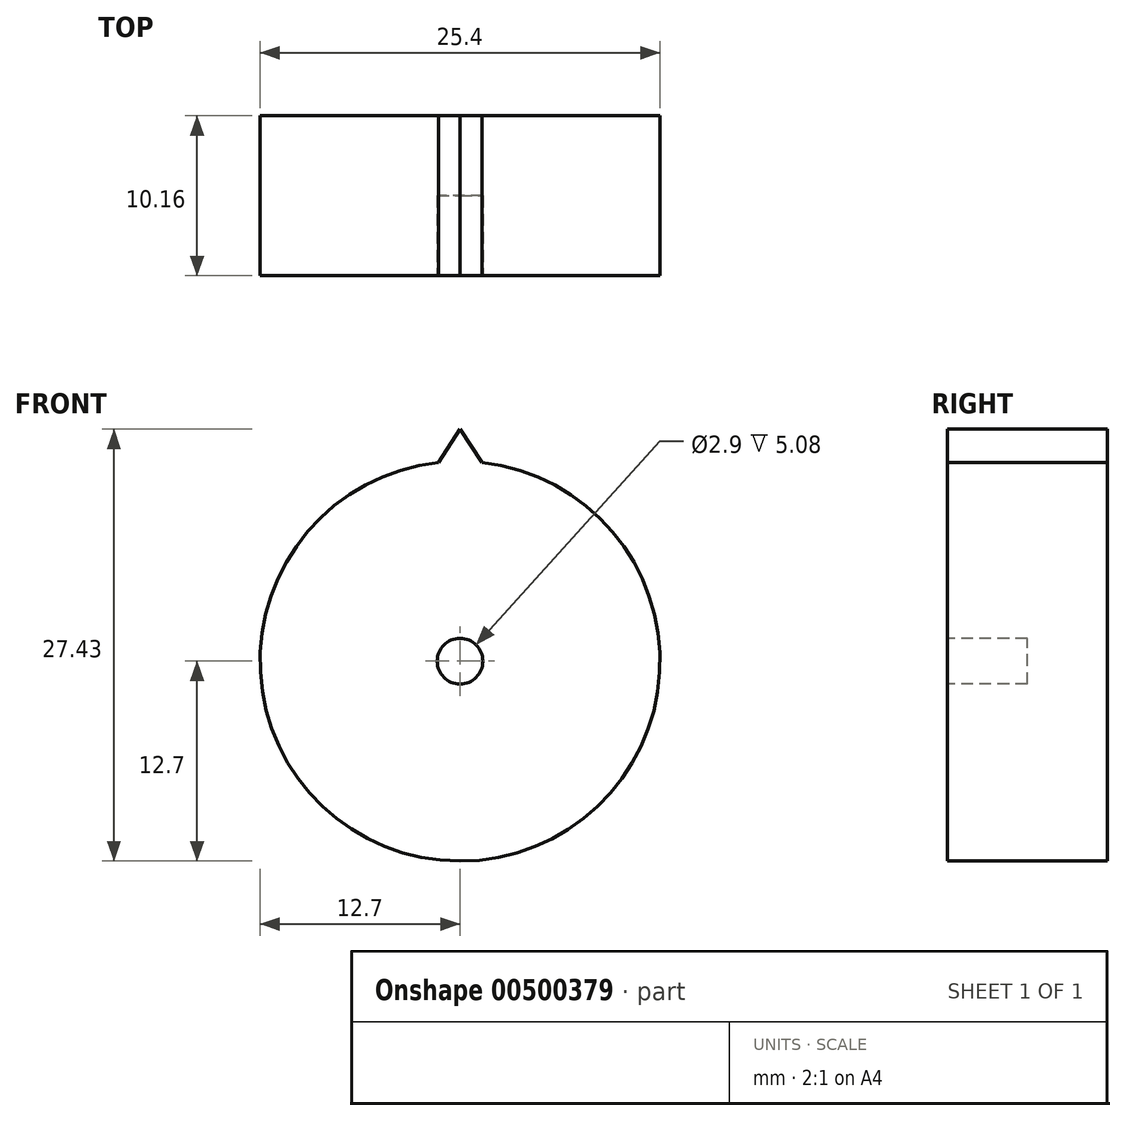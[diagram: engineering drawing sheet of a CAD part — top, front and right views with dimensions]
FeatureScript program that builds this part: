
annotation { "Feature Type Name" : "Feature", "Feature Type Description" : "" }
export const myFeature = defineFeature(function(context is Context, id is Id, definition is map)
    precondition{}
    {
        {
            var Q0;
            Q0=qCreatedBy(makeId("Front.planeOp"),FACE);
            var sketch = newSketch(context, id + "F0", { "sketchPlane" : qUnion([Q0])});
            skCircle(sketch, "E0", {"center": v(0, 0) * mm, "radius": 12.7 * mm});
            skLineSegment(sketch, "E1", {"start": v(-1.36, 12.63) * mm, "end": v(0, 14.73) * mm});
            skLineSegment(sketch, "E2", {"start": v(0, 14.73) * mm, "end": v(1.38, 12.62) * mm});
            skLineSegment(sketch, "E3", {"start": v(-1.36, 12.63) * mm, "end": v(1.38, 12.62) * mm});
            skSolve(sketch);
        }
        {
            var Q0;
            Q0=makeQuery(id+"F0.imprint","IMPRINT",FACE,{"disambiguationData":[TD([[makeQuery(id+"F0.imprint","IMPRINT",EDGE,{"derivedFrom":sQuery(id+"F0.wireOp",EDGE,"E0")}),1.0]])]});
            extrude(context, id + "F1", {"entities" : qUnion([Q0]), "depth" : 10.16 * mm});
        }
        {
            var Q0;
            {var subQ1=sQuery(id+"F0.wireOp",EDGE,"E1");Q0=makeQuery(id+"F0.imprint","IMPRINT",FACE,{"disambiguationData":[TD([[makeQuery(id+"F0.imprint","IMPRINT",EDGE,{"derivedFrom":subQ1}),-1.0]])]});}
            extrude(context, id + "F2", {"entities" : qUnion([Q0]), "operationType" : NewBodyOperationType.ADD, "depth" : 10.16 * mm});
        }
        {
            var Q0;
            {var subQ0=sQuery(id+"F0.wireOp",EDGE,"E2");var subQ1=sQuery(id+"F0.wireOp",EDGE,"E1");var subQ2=sQuery(id+"F0.wireOp",EDGE,"E0");Q0=makeQuery(id+"FW0Evy0XLkxjWks_1.31.F2.boolean.opBoolean","MERGE",FACE,{"derivedFrom":[makeQuery(id+"FW0Evy0XLkxjWks_1.30.F2.boolean.opBoolean","MERGE",FACE,{"derivedFrom":[makeQuery(id+"FW0Evy0XLkxjWks_1.29.F2.boolean.opBoolean","MERGE",FACE,{"derivedFrom":[makeQuery(id+"FW0Evy0XLkxjWks_1.28.F2.boolean.opBoolean","MERGE",FACE,{"derivedFrom":[makeQuery(id+"FW0Evy0XLkxjWks_1.27.F2.boolean.opBoolean","MERGE",FACE,{"derivedFrom":[makeQuery(id+"FW0Evy0XLkxjWks_1.26.F2.boolean.opBoolean","MERGE",FACE,{"derivedFrom":[makeQuery(id+"FW0Evy0XLkxjWks_1.25.F2.boolean.opBoolean","MERGE",FACE,{"derivedFrom":[makeQuery(id+"FW0Evy0XLkxjWks_1.24.F2.boolean.opBoolean","MERGE",FACE,{"derivedFrom":[makeQuery(id+"FW0Evy0XLkxjWks_1.23.F2.boolean.opBoolean","MERGE",FACE,{"derivedFrom":[makeQuery(id+"FW0Evy0XLkxjWks_1.22.F2.boolean.opBoolean","MERGE",FACE,{"derivedFrom":[makeQuery(id+"FW0Evy0XLkxjWks_1.21.F2.boolean.opBoolean","MERGE",FACE,{"derivedFrom":[makeQuery(id+"FW0Evy0XLkxjWks_1.20.F2.boolean.opBoolean","MERGE",FACE,{"derivedFrom":[makeQuery(id+"FW0Evy0XLkxjWks_1.19.F2.boolean.opBoolean","MERGE",FACE,{"derivedFrom":[makeQuery(id+"FW0Evy0XLkxjWks_1.18.F2.boolean.opBoolean","MERGE",FACE,{"derivedFrom":[makeQuery(id+"FW0Evy0XLkxjWks_1.17.F2.boolean.opBoolean","MERGE",FACE,{"derivedFrom":[makeQuery(id+"FW0Evy0XLkxjWks_1.16.F2.boolean.opBoolean","MERGE",FACE,{"derivedFrom":[makeQuery(id+"FW0Evy0XLkxjWks_1.15.F2.boolean.opBoolean","MERGE",FACE,{"derivedFrom":[makeQuery(id+"FW0Evy0XLkxjWks_1.14.F2.boolean.opBoolean","MERGE",FACE,{"derivedFrom":[makeQuery(id+"FW0Evy0XLkxjWks_1.13.F2.boolean.opBoolean","MERGE",FACE,{"derivedFrom":[makeQuery(id+"FW0Evy0XLkxjWks_1.12.F2.boolean.opBoolean","MERGE",FACE,{"derivedFrom":[makeQuery(id+"FW0Evy0XLkxjWks_1.11.F2.boolean.opBoolean","MERGE",FACE,{"derivedFrom":[makeQuery(id+"FW0Evy0XLkxjWks_1.10.F2.boolean.opBoolean","MERGE",FACE,{"derivedFrom":[makeQuery(id+"FW0Evy0XLkxjWks_1.9.F2.boolean.opBoolean","MERGE",FACE,{"derivedFrom":[makeQuery(id+"FW0Evy0XLkxjWks_1.8.F2.boolean.opBoolean","MERGE",FACE,{"derivedFrom":[makeQuery(id+"FW0Evy0XLkxjWks_1.7.F2.boolean.opBoolean","MERGE",FACE,{"derivedFrom":[makeQuery(id+"FW0Evy0XLkxjWks_1.6.F2.boolean.opBoolean","MERGE",FACE,{"derivedFrom":[makeQuery(id+"FW0Evy0XLkxjWks_1.5.F2.boolean.opBoolean","MERGE",FACE,{"derivedFrom":[makeQuery(id+"FW0Evy0XLkxjWks_1.4.F2.boolean.opBoolean","MERGE",FACE,{"derivedFrom":[makeQuery(id+"FW0Evy0XLkxjWks_1.3.F2.boolean.opBoolean","MERGE",FACE,{"derivedFrom":[makeQuery(id+"FW0Evy0XLkxjWks_1.2.F2.boolean.opBoolean","MERGE",FACE,{"derivedFrom":[makeQuery(id+"FW0Evy0XLkxjWks_1.1.F2.boolean.opBoolean","MERGE",FACE,{"derivedFrom":[makeQuery(id+"F2.boolean.opBoolean","MERGE",FACE,{"derivedFrom":[makeQuery(id+"F1.opExtrude","CAP_FACE",FACE,{"disambiguationData":[OSD([subQ2])],"isStart":false}),makeQuery(id+"F2.opExtrude","CAP_FACE",FACE,{"disambiguationData":[OSD([subQ2,subQ1,subQ0])],"isStart":false})]}),makeQuery(id+"FW0Evy0XLkxjWks_1.1.F2.opExtrude","CAP_FACE",FACE,{"disambiguationData":[OSD([subQ2,subQ1,subQ0])],"isStart":false})]}),makeQuery(id+"FW0Evy0XLkxjWks_1.2.F2.opExtrude","CAP_FACE",FACE,{"disambiguationData":[OSD([subQ2,subQ1,subQ0])],"isStart":false})]}),makeQuery(id+"FW0Evy0XLkxjWks_1.3.F2.opExtrude","CAP_FACE",FACE,{"disambiguationData":[OSD([subQ2,subQ1,subQ0])],"isStart":false})]}),makeQuery(id+"FW0Evy0XLkxjWks_1.4.F2.opExtrude","CAP_FACE",FACE,{"disambiguationData":[OSD([subQ2,subQ1,subQ0])],"isStart":false})]}),makeQuery(id+"FW0Evy0XLkxjWks_1.5.F2.opExtrude","CAP_FACE",FACE,{"disambiguationData":[OSD([subQ2,subQ1,subQ0])],"isStart":false})]}),makeQuery(id+"FW0Evy0XLkxjWks_1.6.F2.opExtrude","CAP_FACE",FACE,{"disambiguationData":[OSD([subQ2,subQ1,subQ0])],"isStart":false})]}),makeQuery(id+"FW0Evy0XLkxjWks_1.7.F2.opExtrude","CAP_FACE",FACE,{"disambiguationData":[OSD([subQ2,subQ1,subQ0])],"isStart":false})]}),makeQuery(id+"FW0Evy0XLkxjWks_1.8.F2.opExtrude","CAP_FACE",FACE,{"disambiguationData":[OSD([subQ2,subQ1,subQ0])],"isStart":false})]}),makeQuery(id+"FW0Evy0XLkxjWks_1.9.F2.opExtrude","CAP_FACE",FACE,{"disambiguationData":[OSD([subQ2,subQ1,subQ0])],"isStart":false})]}),makeQuery(id+"FW0Evy0XLkxjWks_1.10.F2.opExtrude","CAP_FACE",FACE,{"disambiguationData":[OSD([subQ2,subQ1,subQ0])],"isStart":false})]}),makeQuery(id+"FW0Evy0XLkxjWks_1.11.F2.opExtrude","CAP_FACE",FACE,{"disambiguationData":[OSD([subQ2,subQ1,subQ0])],"isStart":false})]}),makeQuery(id+"FW0Evy0XLkxjWks_1.12.F2.opExtrude","CAP_FACE",FACE,{"disambiguationData":[OSD([subQ2,subQ1,subQ0])],"isStart":false})]}),makeQuery(id+"FW0Evy0XLkxjWks_1.13.F2.opExtrude","CAP_FACE",FACE,{"disambiguationData":[OSD([subQ2,subQ1,subQ0])],"isStart":false})]}),makeQuery(id+"FW0Evy0XLkxjWks_1.14.F2.opExtrude","CAP_FACE",FACE,{"disambiguationData":[OSD([subQ2,subQ1,subQ0])],"isStart":false})]}),makeQuery(id+"FW0Evy0XLkxjWks_1.15.F2.opExtrude","CAP_FACE",FACE,{"disambiguationData":[OSD([subQ2,subQ1,subQ0])],"isStart":false})]}),makeQuery(id+"FW0Evy0XLkxjWks_1.16.F2.opExtrude","CAP_FACE",FACE,{"disambiguationData":[OSD([subQ2,subQ1,subQ0])],"isStart":false})]}),makeQuery(id+"FW0Evy0XLkxjWks_1.17.F2.opExtrude","CAP_FACE",FACE,{"disambiguationData":[OSD([subQ2,subQ1,subQ0])],"isStart":false})]}),makeQuery(id+"FW0Evy0XLkxjWks_1.18.F2.opExtrude","CAP_FACE",FACE,{"disambiguationData":[OSD([subQ2,subQ1,subQ0])],"isStart":false})]}),makeQuery(id+"FW0Evy0XLkxjWks_1.19.F2.opExtrude","CAP_FACE",FACE,{"disambiguationData":[OSD([subQ2,subQ1,subQ0])],"isStart":false})]}),makeQuery(id+"FW0Evy0XLkxjWks_1.20.F2.opExtrude","CAP_FACE",FACE,{"disambiguationData":[OSD([subQ2,subQ1,subQ0])],"isStart":false})]}),makeQuery(id+"FW0Evy0XLkxjWks_1.21.F2.opExtrude","CAP_FACE",FACE,{"disambiguationData":[OSD([subQ2,subQ1,subQ0])],"isStart":false})]}),makeQuery(id+"FW0Evy0XLkxjWks_1.22.F2.opExtrude","CAP_FACE",FACE,{"disambiguationData":[OSD([subQ2,subQ1,subQ0])],"isStart":false})]}),makeQuery(id+"FW0Evy0XLkxjWks_1.23.F2.opExtrude","CAP_FACE",FACE,{"disambiguationData":[OSD([subQ2,subQ1,subQ0])],"isStart":false})]}),makeQuery(id+"FW0Evy0XLkxjWks_1.24.F2.opExtrude","CAP_FACE",FACE,{"disambiguationData":[OSD([subQ2,subQ1,subQ0])],"isStart":false})]}),makeQuery(id+"FW0Evy0XLkxjWks_1.25.F2.opExtrude","CAP_FACE",FACE,{"disambiguationData":[OSD([subQ2,subQ1,subQ0])],"isStart":false})]}),makeQuery(id+"FW0Evy0XLkxjWks_1.26.F2.opExtrude","CAP_FACE",FACE,{"disambiguationData":[OSD([subQ2,subQ1,subQ0])],"isStart":false})]}),makeQuery(id+"FW0Evy0XLkxjWks_1.27.F2.opExtrude","CAP_FACE",FACE,{"disambiguationData":[OSD([subQ2,subQ1,subQ0])],"isStart":false})]}),makeQuery(id+"FW0Evy0XLkxjWks_1.28.F2.opExtrude","CAP_FACE",FACE,{"disambiguationData":[OSD([subQ2,subQ1,subQ0])],"isStart":false})]}),makeQuery(id+"FW0Evy0XLkxjWks_1.29.F2.opExtrude","CAP_FACE",FACE,{"disambiguationData":[OSD([subQ2,subQ1,subQ0])],"isStart":false})]}),makeQuery(id+"FW0Evy0XLkxjWks_1.30.F2.opExtrude","CAP_FACE",FACE,{"disambiguationData":[OSD([subQ2,subQ1,subQ0])],"isStart":false})]}),makeQuery(id+"FW0Evy0XLkxjWks_1.31.F2.opExtrude","CAP_FACE",FACE,{"disambiguationData":[OSD([subQ2,subQ1,subQ0])],"isStart":false})]});}
            var sketch = newSketch(context, id + "F3", { "sketchPlane" : qUnion([Q0])});
            skCircle(sketch, "E4", {"center": v(0, 0) * mm, "radius": 1.45 * mm});
            skSolve(sketch);
        }
        {
            var Q0;
            Q0 = qSketchRegion(id + "F3", true);
            extrude(context, id + "F4", {"entities" : qUnion([Q0]), "operationType" : NewBodyOperationType.REMOVE, "oppositeDirection" : true, "depth" : 5.08 * mm});
        }
    });
